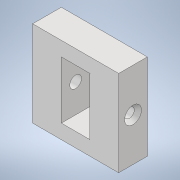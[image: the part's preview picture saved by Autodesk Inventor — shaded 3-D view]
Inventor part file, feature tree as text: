
AUTODESK INVENTOR PART (.ipt)
format: ipt  version: 2022.3 (Build 263350000, 350)  size: 134,656 bytes
history: native  units: mm
features: sketch x4, extrude x2, hole x2
ambient origin geometry x8: Origin, YZ Plane, XZ Plane, XY Plane, X Axis, Y Axis, Z Axis, Center Point
bodies: Solid1 (feature_tree)
feature tree (8):
  extrude  "Extrusion1"  Depth=10.0mm
  extrude  "Extrusion2"  Depth=10.0mm
  hole  "Hole1"  [1 undecoded]
  hole  "Hole2"  [1 undecoded]
  sketch  "Sketch1"  dims[d0=30.0mm d1=10.0mm]
  sketch  "Sketch2"  dims[d2=30.0mm d3=0.0mm d4=10.0mm]
  sketch  "Sketch3"  dims[d5=20.0mm d6=0.0mm d7=0.0mm]
  sketch  "Sketch4"  dims[d8=3.4mm d9=6.0mm d10=5.9mm d11=2.0mm d12=90.0deg d13=10.0mm d14=0.0mm d15=10.0mm d16=3.4mm d17=6.0mm d18=4.1mm d19=5.1mm d20=90.0deg d21=3.9mm d22=0.0mm]
note: 2 required parameter values undecoded (feature->parameter linkage not recoverable at this tier; creation-order binding heuristic only, values carry confidence <= 0.55)
